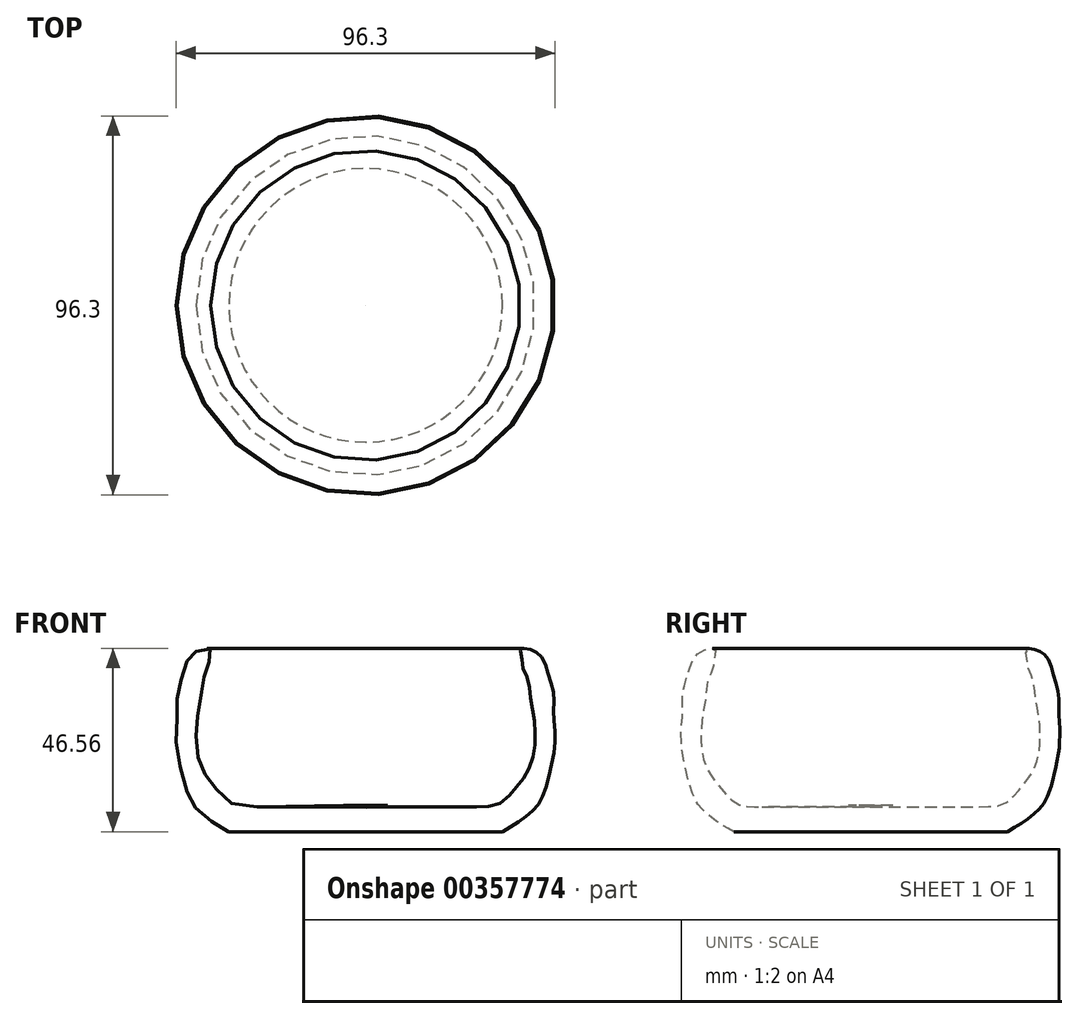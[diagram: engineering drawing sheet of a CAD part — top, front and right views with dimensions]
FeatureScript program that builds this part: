
annotation { "Feature Type Name" : "Feature", "Feature Type Description" : "" }
export const myFeature = defineFeature(function(context is Context, id is Id, definition is map)
    precondition{}
    {
        {
            var Q0;
            Q0=qCreatedBy(makeId("Front.planeOp"),FACE);
            var sketch = newSketch(context, id + "F0", { "sketchPlane" : qUnion([Q0])});
            skFitSpline(sketch, "E0", {"points": [v(34.76, 0) * mm, v(38.92, 2.53) * mm, v(43.08, 5.97) * mm, v(45.07, 9.23) * mm, v(47.25, 17.02) * mm, v(48.15, 24.26) * mm, v(47.79, 30.6) * mm, v(47.79, 34.76) * mm, v(46.52, 39.64) * mm, v(45.07, 43.8) * mm, v(43.63, 45.44) * mm, v(41.63, 46.34) * mm, v(39.46, 46.34) * mm, v(39.64, 44.53) * mm, v(40, 41.63) * mm, v(41.27, 38.74) * mm, v(41.63, 36.2) * mm, v(42.72, 29.14) * mm, v(43.08, 24.44) * mm, v(42.54, 18.83) * mm, v(40.91, 14.84) * mm, v(38.56, 11.59) * mm, v(34.76, 7.6) * mm, v(28.24, 6.34) * mm, v(0, 6.34) * mm, v(0, 6.15) * mm, v(0, 5.97) * mm], "startDerivative": vector(100.54, 57.25) * mm, "endDerivative": vector(-3.77, -22.77) * mm});
            skLineSegment(sketch, "E1", {"start": v(0, 0) * mm, "end": v(0, 5.97) * mm});
            skLineSegment(sketch, "E2", {"start": v(0, 0) * mm, "end": v(34.76, 0) * mm});
            skLineSegment(sketch, "E3", {"start": v(0, 5.97) * mm, "end": v(0, 6.47) * mm});
            skLineSegment(sketch, "E4", {"start": v(0, 6.47) * mm, "end": v(0.93, 6.52) * mm});
            skSolve(sketch);
        }
        {
            var Q0;
            Q0=makeQuery(id+"F0.imprint","IMPRINT",FACE,{"disambiguationData":[TD([[makeQuery(id+"F0.imprint","IMPRINT",EDGE,{"derivedFrom":sQuery(id+"F0.wireOp",EDGE,"E0")}),1.0]])]});
            var Q1;
            Q1=sQuery(id+"F0.wireOp",EDGE,"E1");
            revolve(context, id + "F1", {"entities" : qUnion([Q0]), "axis" : qUnion([Q1]), "revolveType" : RevolveType.FULL});
        }
    });
